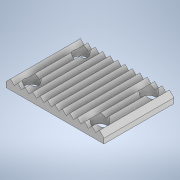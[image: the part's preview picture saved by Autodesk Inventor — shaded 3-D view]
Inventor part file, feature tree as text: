
AUTODESK INVENTOR PART (.ipt)
format: ipt  version: 2020 (Build 240168000, 168)  size: 224,256 bytes
history: native  units: in
note: dims shown in document units (in); Inventor stores cm internally (conversion verified against a paired STEP export)
features: extrude x4, sketch x4, mirror x1
ambient origin geometry x8: Origin, YZ Plane, XZ Plane, XY Plane, X Axis, Y Axis, Z Axis, Center Point
bodies: Solid1 (feature_tree)
feature tree (9):
  extrude  "Extrusion1"  Depth=0.7874in
  extrude  "Extrusion2"  Depth=0.5512in
  mirror  "Mirror1"
  extrude  "Extrusion4"  TaperAngle=135.0deg  [1 undecoded]
  extrude  "Extrusion5"  Depth=0.3937in TaperAngle=0.0deg
  sketch  "Sketch1"  dims[d0=1.1024in d1=0.7874in]
  sketch  "Sketch2"  dims[d2=0.1575in d3=0.0in d4=0.5512in]
  sketch  "Sketch4"  dims[d5=0.0591in d6=135.0deg]
  sketch  "Sketch5"  dims[d7=0.0591in d8=1.9685in d9=0.0in d14=1.9685in d15=0.0in d16=0.1575in d17=0.1575in d18=0.1575in d19=0.1575in d20=0.3937in d21=0.0in]
note: 1 required parameter value undecoded (feature->parameter linkage not recoverable at this tier; creation-order binding heuristic only, values carry confidence <= 0.55)
